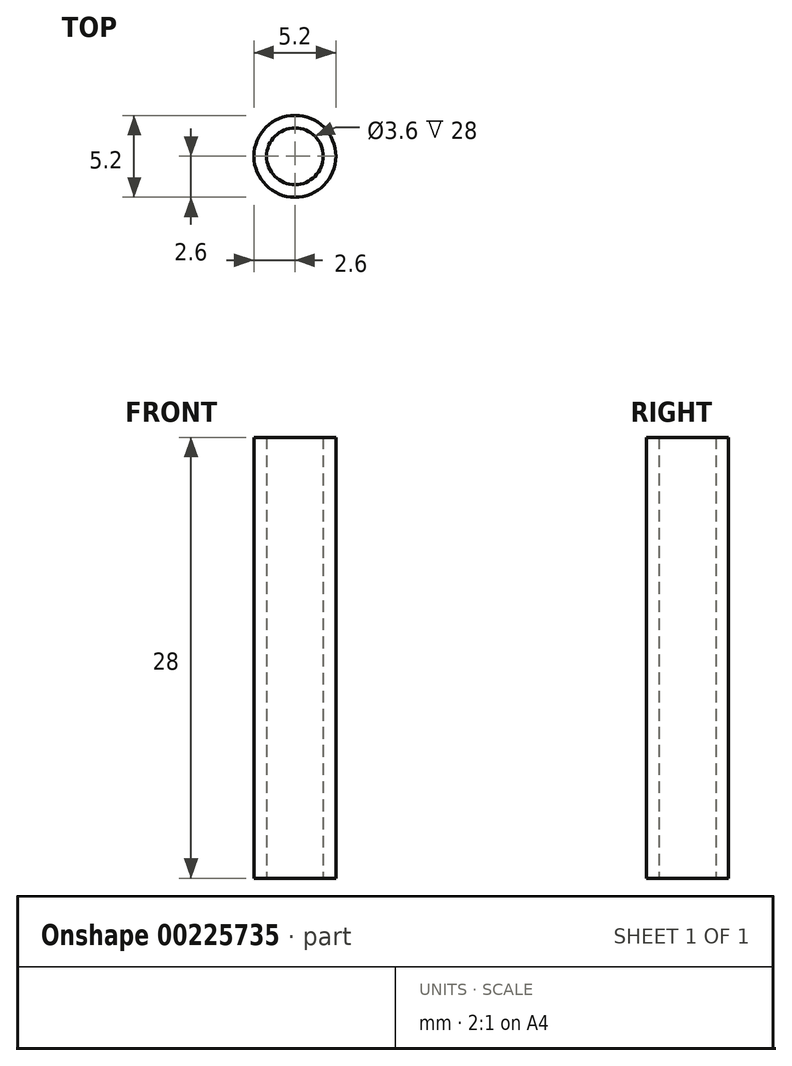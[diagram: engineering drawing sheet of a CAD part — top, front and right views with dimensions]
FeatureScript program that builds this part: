
annotation { "Feature Type Name" : "Feature", "Feature Type Description" : "" }
export const myFeature = defineFeature(function(context is Context, id is Id, definition is map)
    precondition{}
    {
        {
            assignVariable(context, id + "F0", {"name" : "Stand_Height", "anyValue" : 28});
        }
        {
            var Q0;
            Q0=qCreatedBy(makeId("Top.planeOp"),FACE);
            var sketch = newSketch(context, id + "F1", { "sketchPlane" : qUnion([Q0])});
            skCircle(sketch, "E0", {"center": v(0, 0) * mm, "radius": 1.8 * mm});
            skCircle(sketch, "E1", {"center": v(0, 0) * mm, "radius": 2.6 * mm});
            skSolve(sketch);
        }
        {
            var Q0;
            Q0=qSketchRegion(id+"F1",true);
            extrude(context, id + "F2", {"entities" : qUnion([Q0]), "depth" : (getVariable(context, 'Stand_Height')) * mm});
        }
    });
